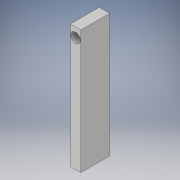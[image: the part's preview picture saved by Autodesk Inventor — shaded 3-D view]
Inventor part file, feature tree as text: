
AUTODESK INVENTOR PART (.ipt)
format: ipt  version: 2019 (Build 230136000, 136)  size: 103,424 bytes
history: native  units: mm
features: sketch x2, sheet_metal_op x1, hole x1, other x1
ambient origin geometry x8: Origin, YZ Plane, XZ Plane, XY Plane, X Axis, Y Axis, Z Axis, Center Point
bodies: Solid1 (feature_tree)
feature tree (5):
  sheet_metal_op  "Face1"
  hole  "Hole1"  [1 undecoded]
  sketch  "Sketch1"  dims[d0=77.0mm d1=18.0mm]
  other  "Plate1"
  sketch  "Sketch2"  dims[d2=6.5mm d3=6.0mm d4=6.0mm d5=4.0mm d6=2.0mm d7=90.0deg d8=6.5mm d9=20.594885mm]
note: 1 required parameter value undecoded (feature->parameter linkage not recoverable at this tier; creation-order binding heuristic only, values carry confidence <= 0.55)
